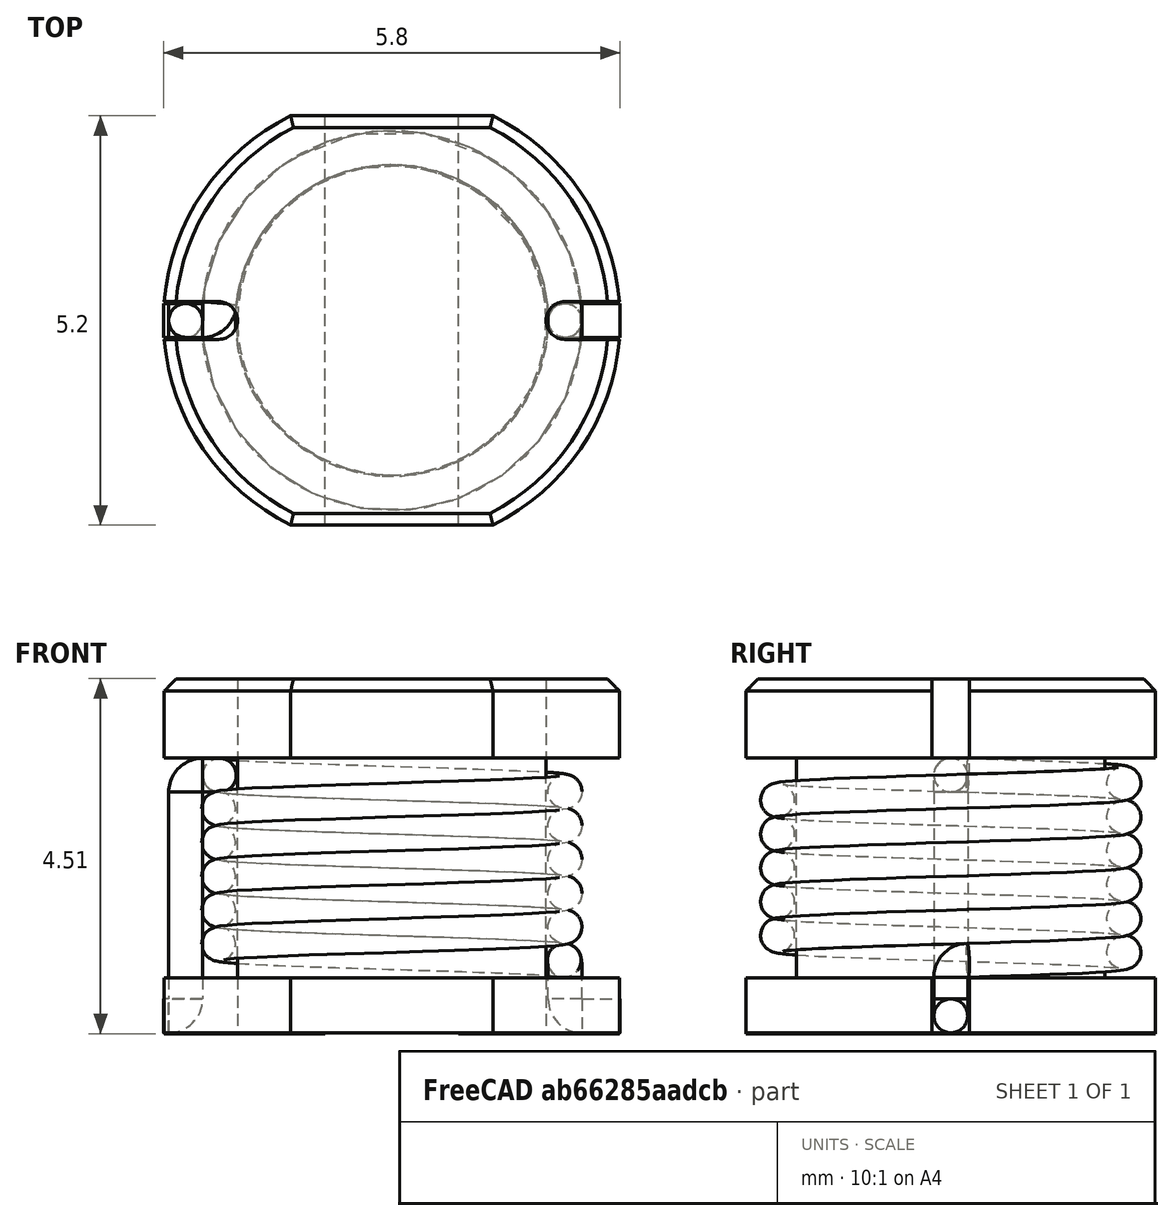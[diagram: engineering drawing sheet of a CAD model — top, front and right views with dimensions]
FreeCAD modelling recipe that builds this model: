
FCSTD DOCUMENT  (FreeCAD 0.17R13528 (Git))
Label: SMD_Inductors_CDxx
License: All rights reserved
LicenseURL: http://en.wikipedia.org/wiki/All_rights_reserved
objects: Part::Part2DObjectPython×19, Part::Sweep×6, Part::Loft×4, Sketcher::SketchObject×3, Part::Extrusion×3, Part::Chamfer×1, Spreadsheet::Sheet×1, Part::Cylinder×1, Part::Helix×1, App::DocumentObjectGroup×1
note: 38 computed .brp shape members not serialized (recipe doc carries the construction recipe); baked Part::Feature solids carry a one-line shape summary decoded from their .brp

FEATURE [Sketcher::SketchObject] Sketch  label="Foundation"
  Placement = pos=(0,0,0) rot=(0,0,1;1.5708rad)
  expr: Constraints.X = Table.X_Foundation
  expr: Constraints.R1 = Table.D_Otv_Vivod / 2
  expr: Constraints.R = Table.D_Foundation / 2
  expr: Constraints.H = Table.D_Coil
  expr: Constraints[27] = Constraints.R
  expr: Constraints[28] = Constraints.R
  sketch-geometry (12):
    g0: LineSegment StartX=-2.6 StartY=1.28452 StartZ=0 EndX=-2.6 EndY=-1.28452 EndZ=0
    g1: LineSegment StartX=2.6 StartY=1.28452 StartZ=0 EndX=2.6 EndY=-1.28452 EndZ=0
    g2: ArcOfCircle CenterX=0 CenterY=0 CenterZ=0 NormalX=0 NormalY=0 NormalZ=1 AngleXU=0 Radius=2.9 StartAngle=1.65365 EndAngle=2.68272
    g3: ArcOfCircle CenterX=0 CenterY=0 CenterZ=0 NormalX=0 NormalY=0 NormalZ=1 AngleXU=0 Radius=2.9 StartAngle=0.458874 EndAngle=1.48794
    g4: ArcOfCircle CenterX=0 CenterY=0 CenterZ=0 NormalX=0 NormalY=0 NormalZ=1 AngleXU=0 Radius=2.9 StartAngle=3.60047 EndAngle=4.62954
    g5: ArcOfCircle CenterX=0 CenterY=0 CenterZ=0 NormalX=0 NormalY=0 NormalZ=1 AngleXU=0 Radius=2.9 StartAngle=4.79524 EndAngle=5.82431
    g6: LineSegment StartX=-0.24 StartY=-2.89005 StartZ=0 EndX=-0.24 EndY=-2.2 EndZ=0
    g7: LineSegment StartX=0.24 StartY=-2.89005 StartZ=0 EndX=0.24 EndY=-2.2 EndZ=0
    g8: LineSegment StartX=-0.24 StartY=2.89005 StartZ=0 EndX=-0.24 EndY=2.2 EndZ=0
    g9: LineSegment StartX=0.24 StartY=2.89005 StartZ=0 EndX=0.24 EndY=2.2 EndZ=0
    g10: ArcOfCircle CenterX=0 CenterY=2.2 CenterZ=0 NormalX=0 NormalY=0 NormalZ=1 AngleXU=0 Radius=0.24 StartAngle=3.14159 EndAngle=6.28319
    g11: ArcOfCircle CenterX=0 CenterY=-2.2 CenterZ=0 NormalX=0 NormalY=0 NormalZ=1 AngleXU=0 Radius=0.24 StartAngle=0 EndAngle=3.14159
  constraints (37):
    c: Vertical(g1)
    c: DistanceX(g0,g1) = 5.2  'X'
    c: Coincident(g2,g-1)
    c: Coincident(g2,g0)
    c: Coincident(g3,g-1)
    c: Coincident(g3,g1)
    c: Coincident(g4,g-1)
    c: Coincident(g4,g0)
    c: Coincident(g5,g-1)
    c: Coincident(g5,g1)
    c: Coincident(g6,g4)
    c: Vertical(g6)
    c: Coincident(g7,g5)
    c: Vertical(g7)
    c: Coincident(g8,g2)
    c: Vertical(g8)
    c: Coincident(g9,g3)
    c: Vertical(g9)
    c: PointOnObject(g10,g-2)
    c: Coincident(g10,g9)
    c: Coincident(g10,g8)
    c: Coincident(g11,g6)
    c: Coincident(g11,g7)
    c: Radius(g10) = 0.24  'R1'
    c: Equal(g10,g11)
    c: Symmetric(g11,g10,g-1)
    c: Radius(g3) = 2.9  'R'
    c: Radius(g2) = 2.9
    c: Radius(g5) = 2.9
    c: Equal(g7,g6)
    c: Equal(g6,g8)
    c: Equal(g8,g9)
    c: Symmetric(g6,g8,g-1)
    c: DistanceY(g11,g10) = 4.4  'H'
    c: DistanceY(g1,g0) = 0
    c: Symmetric(g0,g0,g-1)
    c: DistanceY(g8,g10) = 0
FEATURE [Part::Extrusion] Extrude  label="Foundation_Solid"
  Base = -> Sketch
  Dir = (0,0,1)
  DirMode = 2
  FaceMakerClass = Part::FaceMakerBullseye
  LengthFwd = 0.7
  LengthRev = 0
  Solid = true
  Symmetric = false
  expr: LengthFwd = Table.Th_Foundation
FEATURE [Sketcher::SketchObject] Sketch001  label="Top"
  Placement = pos=(0,0,3.495) rot=(0,0,1;1.5708rad)
  expr: Placement.Base.z = Table.H_Coil - Table.Th_Top
  expr: Constraints[26] = Foundation.Constraints.R
  expr: Constraints[28] = Foundation.Constraints.R
  expr: Constraints[27] = Foundation.Constraints.R
  expr: Constraints[33] = Foundation.Constraints.H
  expr: Constraints[23] = Foundation.Constraints.R1
  expr: Constraints[1] = Foundation.Constraints.X
  sketch-geometry (12):
    g0: LineSegment StartX=-2.6 StartY=1.28452 StartZ=0 EndX=-2.6 EndY=-1.28452 EndZ=0
    g1: LineSegment StartX=2.6 StartY=1.28452 StartZ=0 EndX=2.6 EndY=-1.28452 EndZ=0
    g2: ArcOfCircle CenterX=0 CenterY=0 CenterZ=0 NormalX=0 NormalY=0 NormalZ=1 AngleXU=0 Radius=2.9 StartAngle=1.65365 EndAngle=2.68272
    g3: ArcOfCircle CenterX=0 CenterY=0 CenterZ=0 NormalX=0 NormalY=0 NormalZ=1 AngleXU=0 Radius=2.9 StartAngle=0.458874 EndAngle=1.48794
    g4: ArcOfCircle CenterX=0 CenterY=0 CenterZ=0 NormalX=0 NormalY=0 NormalZ=1 AngleXU=0 Radius=2.9 StartAngle=3.60047 EndAngle=4.62954
    g5: ArcOfCircle CenterX=0 CenterY=0 CenterZ=0 NormalX=0 NormalY=0 NormalZ=1 AngleXU=0 Radius=2.9 StartAngle=4.79524 EndAngle=5.82431
    g6: LineSegment StartX=-0.24 StartY=-2.89005 StartZ=0 EndX=-0.24 EndY=-2.2 EndZ=0
    g7: LineSegment StartX=0.24 StartY=-2.89005 StartZ=0 EndX=0.24 EndY=-2.2 EndZ=0
    g8: LineSegment StartX=-0.24 StartY=2.89005 StartZ=0 EndX=-0.24 EndY=2.2 EndZ=0
    g9: LineSegment StartX=0.24 StartY=2.89005 StartZ=0 EndX=0.24 EndY=2.2 EndZ=0
    g10: ArcOfCircle CenterX=0 CenterY=2.2 CenterZ=0 NormalX=0 NormalY=0 NormalZ=1 AngleXU=0 Radius=0.24 StartAngle=3.14159 EndAngle=6.28319
    g11: ArcOfCircle CenterX=0 CenterY=-2.2 CenterZ=0 NormalX=0 NormalY=0 NormalZ=1 AngleXU=0 Radius=0.24 StartAngle=0 EndAngle=3.14159
  constraints (37):
    c: Vertical(g1)
    c: DistanceX(g0,g1) = 5.2
    c: Coincident(g2,g-1)
    c: Coincident(g2,g0)
    c: Coincident(g3,g-1)
    c: Coincident(g3,g1)
    c: Coincident(g4,g-1)
    c: Coincident(g4,g0)
    c: Coincident(g5,g-1)
    c: Coincident(g5,g1)
    c: Coincident(g6,g4)
    c: Vertical(g6)
    c: Coincident(g7,g5)
    c: Vertical(g7)
    c: Coincident(g8,g2)
    c: Vertical(g8)
    c: Coincident(g9,g3)
    c: Vertical(g9)
    c: PointOnObject(g10,g-2)
    c: Coincident(g10,g9)
    c: Coincident(g10,g8)
    c: Coincident(g11,g6)
    c: Coincident(g11,g7)
    c: Radius(g10) = 0.24
    c: Equal(g10,g11)
    c: Symmetric(g11,g10,g-1)
    c: Radius(g3) = 2.9
    c: Radius(g2) = 2.9
    c: Radius(g5) = 2.9
    c: Equal(g7,g6)
    c: Equal(g6,g8)
    c: Equal(g8,g9)
    c: Symmetric(g6,g8,g-1)
    c: DistanceY(g11,g10) = 4.4
    c: DistanceY(g1,g0) = 0
    c: Symmetric(g0,g0,g-1)
    c: DistanceY(g8,g10) = 0
FEATURE [Part::Extrusion] Extrude001  label="Top_Solid"
  Base = -> Sketch001
  Dir = (0,0,1)
  DirMode = 2
  FaceMakerClass = Part::FaceMakerBullseye
  LengthFwd = 1
  LengthRev = 0
  Solid = true
  Symmetric = false
  expr: LengthFwd = Table.Th_Top
FEATURE [Part::Chamfer] Chamfer  label="Top_Chamfer_Solid"
  Base = -> Extrude001
  Edges = 6 edges r=0.15: [Edge4,Edge7,Edge10,Edge22,Edge25,Edge28]
FEATURE [Spreadsheet::Sheet] Spreadsheet  label="Table"
  cells = A1=Диаметр катушки по центу провода; B1(D_Coil)==Table.X_Foundation - 0.80000000000000004mm; C1="D_Coil"; D1=Diameter of coil in the center of the wire; A2=Толщина провода; B2(Th_Wire)==0.42999999999999999mm; C2="Th_Wire"; D2=Thickness of wire; A3=Основание; A4=Толщина основания; B4(Th_Foundation)==0.69999999999999996mm; C4="Th_Foundation"; D4=Foundation height; A5=Диаметр основания; B5(D_Foundation)==5.7999999999999998mm; C5="D_Foundation"; D5=Foundation diameter; A6=Растояние между фасками; B6(X_Foundation)==5.2000000000000002mm; C6="X_Foundation"; D6=Foundation "A" dimension; A7=Диаметр отверстий для выводов (расчитываеться, можно ввести); B7(D_Otv_Vivod)==Th_Wire + 0.050000000000000003mm; C7="D_Otv_Vivod"; D7=Diameter of holes for pinouts (calculated, can be setted); A8=Крышка; A9=Толщина крышки; B9(Th_Top)==1mm; C9="Th_Top"; D9=Top height; A10=Высота катушки (расчитывается); B10(H_Coil)==Table.Th_Foundation + (Table.KolvoVitkov + 1.5) * Table.Th_Wire + Table.Th_Top; C10="H_Coil"; D10=Inductor height (calculated); A12=Количество витков; B12(KolvoVitkov)=5; C12="KolvoVitkov"; D12=Number of turns; A13=Ширина площадок; B13(E_dimension)==Table.X_Foundation; C13="E_dimension"; D13=Pinouts "E" dimension; A14=Отступ площадок от центра; B14(F_dimension)==1.7mm; C14="F_dimension"; D14=Pinouts "E" dimension; A15=Длина окружности в плоскости (от диметра катушки); B15(L_Okr)==pi * Table.D_Coil; C15="L_Okr"; D15=Circumference; A16=Длина провода на один виток; B16(L_1Wire)==sqrt(Table.L_Okr * Table.L_Okr + Table.Th_Wire * Table.Th_Wire); C16="L_1Wire"; A17=На сколько повернуть круг; B17(Ugol1)==90deg - asin(Table.Th_Wire / Table.L_1Wire); C17="Ugol1"; A18=Узнаем на сколько повернуть спираль против час стрелки вокруг оси Z; A19=Повернуть спираль вокруг OZ на; B19(Ugol2)==180deg - 2 * acos(Table.Th_Wire / 2 / Table.D_Coil); C19="Ugol2"; A20=Спираль надо приподнять вот на эту величину; B20(DeltaH)==Table.Th_Wire * Table.Ugol2 / 360deg; C20="DeltaH"; D20=Спираль станет короче на величину в 2 раза большую; A22=Расчеты координат и поворота круга для постройки спирали провода; A23=Поворот на угол фи вокруг оси OZ; B23(fi)==Table.Ugol2; C23="fi"; A24=Поворот на угол тета вокруг повернутой оси OU; B24(teta)==90deg + asin(Table.Th_Wire / Table.L_1Wire); C24="teta"; A25=Поворот на угол пси вокруг повернутой оси OW; B25(psii)==0deg; C25="psii" Если сделаем провод прям. сечения; A26=Результирующая матрица поворота; A27(M_11)==cos(Table.fi) * cos(Table.psii) - sin(Table.fi) * cos(Table.teta) * sin(Table.psii); B27(M_21)==-cos(Table.fi) * sin(Table.psii) - sin(Table.fi) * cos(Table.teta) * cos(Table.psii); C27(M_31)==sin(Table.fi) * sin(Table.teta); A28(M_12)==sin(Table.fi) * cos(Table.psii) + cos(Table.fi) * cos(Table.teta) * sin(Table.psii); B28(M_22)==-sin(Table.fi) * sin(Table.psii) + cos(Table.fi) * cos(Table.teta) * cos(Table.psii); C28(M_32)==-cos(Table.fi) * sin(Table.teta); A29(M_13)==sin(Table.teta) * sin(Table.psii); B29(M_23)==sin(Table.teta) * cos(Table.psii); C29(M_33)==cos(Table.teta); A30=Угол на который надо поворачивать; B30(Ugol3)==acos((Table.M_11 + Table.M_22 + Table.M_33 - 1) * 0.5); C30="Ugol3"; A31=Вектор вокруг которого надо поворачивать, X; B31(V_X)==-1 / (2 * sin(Table.Ugol3)) * (Table.M_32 - Table.M_23); C31="V_X"; A32=Вектор вокруг которого надо поворачивать, Y; B32(V_Y)==-1 / (2 * sin(Table.Ugol3)) * (Table.M_13 - Table.M_31); C32="V_Y"; A33=Вектор вокруг которого надо поворачивать, Z; B33(V_Z)==-1 / (2 * sin(Table.Ugol3)) * (Table.M_21 - Table.M_12); C33="V_Z"; A34=Кординаты вектора до центра круга до/после пов., X; B34==Table.D_Coil / 2; C34(Center1_X)==Table.D_Coil / 2 * cos(Table.fi); A35=Кординаты вектора до центра круга до/после пов., Y; B35==0mm; C35(Center1_Y)==Table.D_Coil / 2 * sin(Table.fi); A36=Кординаты вектора до центра круга до/после пов., Z; B36==Table.Th_Foundation + Table.Th_Wire / 2; C36(Center1_Z)==Table.Th_Foundation + Th_Wire / 2 + Table.DeltaH; A37=Расчет координат поворота дуги; A38=Поворот на угол фи вокруг оси OZ; B38(fi2)==-Table.Ugol2; C38="fi2"; A39=Поворот на угол тета вокруг повернутой оси OU; B39(teta2)==90deg - asin(Table.Th_Wire / Table.L_1Wire); C39="teta2"; A40=Поворот на угол пси вокруг повернутой оси OW; B40(psi2)==0deg; C40="psi2"; A41=Результирующая матрица поворота Дуга в начале; A42==cos(fi2) * cos(psi2) - sin(fi2) * cos(teta2) * sin(psi2); B42==-cos(fi2) * sin(psi2) - sin(fi2) * cos(teta2) * cos(psi2); C42==sin(fi2) * sin(teta2); A43==sin(fi2) * cos(psi2) + cos(fi2) * cos(teta2) * sin(psi2); B43==-sin(fi2) * sin(psi2) + cos(fi2) * cos(teta2) * cos(psi2); C43==-cos(fi2) * sin(teta2); A44==sin(teta2) * sin(psi2); B44==sin(teta2) * cos(psi2); C44==cos(teta2); A45=Угол на который надо поворачивать; B45(Ugol4)==acos((A42 + B43 + C44 - 1) * 0.5); C45="Ugol4"; A46=Вектор вокруг которого надо поворачивать, X; B46(V2_X)==-1 / (2 * sin(Table.Ugol4)) * (C43 - B44); C46="V2_X"; A47=Вектор вокруг которого надо поворачивать, Y; B47(V2_Y)==-1 / (2 * sin(Ugol4)) * (A44 - C42); C47="V2_Y"; A48=Вектор вокруг которого надо поворачивать, Z; B48(V2_Z)==-1 / (2 * sin(Ugol4)) * (B42 - A43); C48="V2_Z"; A49=Результирующая матрица поворота Дуга в конце; B49(teta3)==asin(Th_Wire / sqrt(L_Okr * L_Okr + Th_Wire * Th_Wire)); C49="teta3"; A50==cos(90deg + fi) * cos(psi2) - sin(90deg + fi) * cos(90deg) * sin(psi2); B50==-cos(90deg + fi) * sin(psi2) - sin(90deg + fi) * cos(90deg) * cos(psi2); C50==sin(90deg + fi) * sin(90deg); A51==sin(90deg + fi) * cos(psi2) + cos(90deg + fi) * cos(90deg) * sin(psi2); B51==-sin(90deg + fi) * sin(psi2) + cos(90deg + fi) * cos(90deg) * cos(psi2); C51==-cos(90deg + fi) * sin(90deg); A52==sin(90deg) * sin(psi2); B52==sin(90deg) * cos(psi2); C52==cos(90deg); A53=Угол на который надо поворачивать; B53(Ugol5)==acos((A50 + B51 + C52 - 1) * 0.5); C53="Ugol5"; A54=Вектор вокруг которого надо поворачивать, X; B54(V3_X)==-1 / (2 * sin(Ugol5)) * (C51 - B52); C54="V3_X"; A55=Вектор вокруг которого надо поворачивать, Y; B55(V3_Y)==-1 / (2 * sin(Ugol5)) * (A52 - C50); C55="V3_Y"; A56=Вектор вокруг которого надо поворачивать, Z; B56(V3_Z)==-1 / (2 * sin(Ugol5)) * (B50 - A51); C56="V3_Z"
FEATURE [Part::Cylinder] Cylinder
  Angle = 360
  AttacherType = Attacher::AttachEngine3D
  Height = 2.795
  Placement = pos=(0,0,0.7) rot=(0,0,1;0rad)
  Radius = 1.96
  expr: Height = Table.H_Coil - Table.Th_Foundation - Table.Th_Top
  expr: Radius = (Table.D_Coil - Table.D_Otv_Vivod) / 2
  expr: Placement.Base.z = Table.Th_Foundation
FEATURE [Part::Helix] Helix
  Angle = 0
  AttacherType = Attacher::AttachEngine3D
  Height = 2.35162
  LocalCoord = 0
  Pitch = 0.43
  Placement = pos=(0,0,0.921691) rot=(0,0,1;0.097766rad)
  Radius = 2.2
  Style = 1
  expr: Placement.Rotation.Angle = Table.Ugol2
  expr: Pitch = Table.Th_Wire
  expr: Height = Table.H_Coil - Table.Th_Foundation - Table.Th_Top - Table.Th_Wire - Table.DeltaH * 2
  expr: Placement.Base.z = Table.Th_Foundation + Table.Th_Wire / 2 + Table.DeltaH
  expr: Radius = Table.D_Coil / 2
FEATURE [Part::Part2DObjectPython] Circle001  label="Circle2"  # Draft 2D object (typed FeaturePython)
  FirstAngle = 0
  LastAngle = 0
  MakeFace = true
  Placement = pos=(2.2,0,0.706691) rot=(0,0,1;0rad)
  Radius = 0.215
  expr: Radius = Table.Th_Wire / 2
  expr: Placement.Base.z = Table.Th_Foundation + Table.DeltaH
  expr: Placement.Base.x = Table.D_Coil / 2
FEATURE [Part::Part2DObjectPython] Circle002  label="Circle3"  # Draft 2D object (typed FeaturePython)
  FirstAngle = 0
  LastAngle = 0
  MakeFace = true
  Placement = pos=(2.2,0,0.43) rot=(0,0,1;0rad)
  Radius = 0.215
  expr: Radius = Table.Th_Wire / 2
  expr: Placement.Base.z = Table.Th_Wire
  expr: Placement.Base.x = Table.D_Coil / 2
FEATURE [Part::Part2DObjectPython] Circle003  label="Circle4"  # Draft 2D object (typed FeaturePython)
  FirstAngle = 0
  LastAngle = 0
  MakeFace = true
  Placement = pos=(2.415,0,0.215) rot=(0,1,0;1.5708rad)
  Radius = 0.215
  expr: Placement.Base.x = (Table.D_Coil + Table.Th_Wire) / 2
  expr: Radius = Table.Th_Wire / 2
  expr: Placement.Base.z = Table.Th_Wire / 2
FEATURE [Part::Part2DObjectPython] Circle004  label="RotateCircle"  # Draft 2D object (typed FeaturePython)
  FirstAngle = 0
  LastAngle = 0
  MakeFace = true
  Placement = pos=(2.18949,0.214743,0.921691) rot=(0.997687,0.048806,0.047309;1.60421rad)
  Radius = 0.215
  expr: Placement.Base.x = Table.Center1_X
  expr: Placement.Base.y = Table.Center1_Y
  expr: Placement.Rotation.Axis.z = Table.V_Z
  expr: Placement.Rotation.Axis.y = Table.V_Y
  expr: Placement.Base.z = Table.Center1_Z
  expr: Placement.Rotation.Angle = Table.Ugol3
  expr: Placement.Rotation.Axis.x = Table.V_X
  expr: Radius = Table.Th_Wire / 2
FEATURE [Part::Part2DObjectPython] Arc  label="Arc2"  # Draft 2D object (typed FeaturePython)
  FirstAngle = 90
  LastAngle = 180
  MakeFace = true
  Placement = pos=(2.18949,0.214743,0.706691) rot=(0.539926,0.595289,0.595072;2.15173rad)
  Radius = 0.215
  expr: Placement.Base.y = Table.Center1_Y
  expr: Radius = Table.Th_Wire / 2
  expr: Placement.Rotation.Axis.z = Table.V3_Z
  expr: Placement.Rotation.Axis.y = Table.V3_Y
  expr: Placement.Rotation.Angle = Table.Ugol5
  expr: Placement.Rotation.Axis.x = Table.V3_X
  expr: Placement.Base.z = Table.Th_Foundation + Table.DeltaH
  expr: Placement.Base.x = Table.Center1_X
FEATURE [Part::Part2DObjectPython] Circle005  label="RotateCircle2"  # Draft 2D object (typed FeaturePython)
  FirstAngle = 0
  LastAngle = 0
  MakeFace = true
  Placement = pos=(2.18949,0.214743,0.921691) rot=(0.997687,0.048806,0.047309;1.60421rad)
  Radius = 0.215
  expr: Placement.Base.y = Table.Center1_Y
  expr: Placement.Rotation.Axis.z = Table.V_Z
  expr: Placement.Rotation.Axis.y = Table.V_Y
  expr: Placement.Base.z = Table.Center1_Z
  expr: Placement.Base.x = Table.Center1_X
  expr: Placement.Rotation.Angle = Table.Ugol3
  expr: Placement.Rotation.Axis.x = Table.V_X
  expr: Radius = Table.Th_Wire / 2
FEATURE [Part::Sweep] Sweep001  label="Wire4"
  Frenet = true
  Sections = -> [Circle005,Circle001]
  Solid = true
  Spine = -> Arc [Edge1]
  Transition = 1
FEATURE [Part::Part2DObjectPython] Circle006  label="Circle5"  # Draft 2D object (typed FeaturePython)
  FirstAngle = 0
  LastAngle = 0
  MakeFace = true
  Placement = pos=(2.2,0,0.706691) rot=(0,0,1;0rad)
  Radius = 0.215
  expr: Radius = Table.Th_Wire / 2
  expr: Placement.Base.z = Table.Th_Foundation + Table.DeltaH
  expr: Placement.Base.x = Table.D_Coil / 2
FEATURE [Part::Loft] Loft  label="Wire3"
  Closed = false
  MaxDegree = 5
  Ruled = false
  Sections = -> [Circle002,Circle006]
  Solid = true
FEATURE [Part::Part2DObjectPython] Circle007  label="Circle6"  # Draft 2D object (typed FeaturePython)
  FirstAngle = 0
  LastAngle = 0
  MakeFace = true
  Placement = pos=(2.2,0,0.43) rot=(0,0,1;0rad)
  Radius = 0.215
  expr: Radius = Table.Th_Wire / 2
  expr: Placement.Base.z = Table.Th_Wire
  expr: Placement.Base.x = Table.D_Coil / 2
FEATURE [Part::Part2DObjectPython] Arc001  label="Arc1"  # Draft 2D object (typed FeaturePython)
  FirstAngle = 180
  LastAngle = 270
  MakeFace = true
  Placement = pos=(2.415,0,0.43) rot=(1,0,0;1.5708rad)
  Radius = 0.215
  expr: Placement.Base.z = Table.Th_Wire
  expr: Placement.Base.x = Table.D_Coil / 2 + Table.Th_Wire / 2
  expr: Radius = Table.Th_Wire / 2
FEATURE [Part::Sweep] Sweep002  label="Wire2"
  Frenet = true
  Sections = -> [Circle007,Circle003]
  Solid = true
  Spine = -> Arc001 [Edge1]
  Transition = 1
FEATURE [Part::Sweep] Sweep  label="Wire5"
  Frenet = true
  Sections = -> [Circle004]
  Solid = true
  Spine = -> Helix [Edge1,Edge2,Edge3,Edge4,Edge5,Edge6]
  Transition = 1
FEATURE [Part::Part2DObjectPython] Arc002  label="Arc3"  # Draft 2D object (typed FeaturePython)
  FirstAngle = 270
  LastAngle = 360
  MakeFace = true
  Placement = pos=(-2.40449,0.214743,3.27331) rot=(0,0,1;0rad)
  Radius = 0.215
  expr: Radius = Table.Th_Wire / 2
  expr: Placement.Base.y = Table.Center1_Y
  expr: Placement.Base.z = Table.H_Coil - Table.Th_Top - Table.Th_Wire / 2 - Table.DeltaH
  expr: Placement.Base.x = -Table.Center1_X - Table.Th_Wire / 2
FEATURE [Part::Part2DObjectPython] Circle  # Draft 2D object (typed FeaturePython)
  FirstAngle = 0
  LastAngle = 0
  MakeFace = true
  Placement = pos=(-2.40449,0,3.27331) rot=(0.57735,0.57735,0.57735;2.0944rad)
  Radius = 0.215
  expr: Radius = Table.Th_Wire / 2
  expr: Placement.Base.z = Table.H_Coil - Table.Th_Top - Table.Th_Wire / 2 - Table.DeltaH
  expr: Placement.Base.x = -Table.Center1_X - Table.Th_Wire / 2
FEATURE [Part::Part2DObjectPython] Circle008  label="RotateCircle3"  # Draft 2D object (typed FeaturePython)
  FirstAngle = 0
  LastAngle = 0
  MakeFace = true
  Placement = pos=(-2.18949,0.214743,3.27331) rot=(0.997539,-0.048799,-0.050338;1.54216rad)
  Radius = 0.215
  expr: Placement.Rotation.Axis.z = Table.V2_Z
  expr: Placement.Rotation.Axis.y = Table.V2_Y
  expr: Placement.Rotation.Angle = Table.Ugol4
  expr: Placement.Rotation.Axis.x = Table.V2_X
  expr: Placement.Base.y = Table.Center1_Y
  expr: Radius = Table.Th_Wire / 2
  expr: Placement.Base.z = Table.H_Coil - Table.Th_Top - Table.Th_Wire / 2 - Table.DeltaH
  expr: Placement.Base.x = -Table.Center1_X
FEATURE [Part::Sweep] Sweep003  label="Wire6"
  Frenet = true
  Sections = -> [Circle008,Circle]
  Solid = true
  Spine = -> Arc002 [Edge1]
  Transition = 1
FEATURE [Part::Part2DObjectPython] Arc003  label="Arc4"  # Draft 2D object (typed FeaturePython)
  FirstAngle = 90
  LastAngle = 180
  MakeFace = true
  Placement = pos=(-2.40449,0,3.05831) rot=(1,0,0;1.5708rad)
  Radius = 0.215
  expr: Placement.Base.z = Table.H_Coil - Table.Th_Top - Table.Th_Wire - Table.DeltaH
  expr: Radius = Table.Th_Wire / 2
  expr: Placement.Base.x = -Table.Center1_X - Table.Th_Wire / 2
FEATURE [Part::Part2DObjectPython] Circle009  # Draft 2D object (typed FeaturePython)
  FirstAngle = 0
  LastAngle = 0
  MakeFace = true
  Placement = pos=(-2.61949,0,3.05831) rot=(0,0,1;0rad)
  Radius = 0.215
  expr: Radius = Table.Th_Wire / 2
  expr: Placement.Base.z = Table.H_Coil - Table.Th_Top - Table.Th_Wire - Table.DeltaH
  expr: Placement.Base.x = -Table.Center1_X - Table.Th_Wire
FEATURE [Part::Part2DObjectPython] Circle010  # Draft 2D object (typed FeaturePython)
  FirstAngle = 0
  LastAngle = 0
  MakeFace = true
  Placement = pos=(-2.61949,0,0.43) rot=(0,0,1;0rad)
  Radius = 0.215
  expr: Radius = Table.Th_Wire / 2
  expr: Placement.Base.z = Table.Th_Wire
  expr: Placement.Base.x = -Table.Center1_X - Table.Th_Wire
FEATURE [Part::Sweep] Sweep004  label="Wire7"
  Frenet = true
  Sections = -> [Circle,Circle009]
  Solid = true
  Spine = -> Arc003 [Edge1]
  Transition = 1
FEATURE [Part::Part2DObjectPython] Circle011  # Draft 2D object (typed FeaturePython)
  FirstAngle = 0
  LastAngle = 0
  MakeFace = true
  Placement = pos=(-2.83449,0,0.215) rot=(0,1,0;1.5708rad)
  Radius = 0.215
  expr: Radius = Table.Th_Wire / 2
  expr: Placement.Base.z = Table.Th_Wire / 2
  expr: Placement.Base.x = -Table.Center1_X - Table.Th_Wire * 3 / 2
FEATURE [Part::Loft] Loft001  label="Wire8"
  Closed = false
  MaxDegree = 5
  Ruled = false
  Sections = -> [Circle009,Circle010]
  Solid = true
FEATURE [Part::Part2DObjectPython] Arc004  label="Arc5"  # Draft 2D object (typed FeaturePython)
  FirstAngle = 270
  LastAngle = 360
  MakeFace = true
  Placement = pos=(-2.83449,0,0.43) rot=(1,0,0;1.5708rad)
  Radius = 0.215
  expr: Placement.Base.z = Table.Th_Wire
  expr: Radius = Table.Th_Wire / 2
  expr: Placement.Base.x = -Table.Center1_X - Table.Th_Wire * 3 / 2
FEATURE [Part::Sweep] Sweep005  label="Wire9"
  Frenet = true
  Sections = -> [Circle010,Circle011]
  Solid = true
  Spine = -> Arc004 [Edge1]
  Transition = 1
FEATURE [Part::Part2DObjectPython] Circle012  # Draft 2D object (typed FeaturePython)
  FirstAngle = 0
  LastAngle = 0
  MakeFace = true
  Placement = pos=(2.9,0,0.215) rot=(0,1,0;1.5708rad)
  Radius = 0.215
  expr: Placement.Base.x = Table.D_Foundation / 2
  expr: Radius = Table.Th_Wire / 2
  expr: Placement.Base.z = Table.Th_Wire / 2
FEATURE [Part::Loft] Loft002  label="Wire1"
  Closed = false
  MaxDegree = 5
  Ruled = false
  Sections = -> [Circle003,Circle012]
  Solid = true
FEATURE [Part::Part2DObjectPython] Circle013  # Draft 2D object (typed FeaturePython)
  FirstAngle = 0
  LastAngle = 0
  MakeFace = true
  Placement = pos=(-2.9,0,0.215) rot=(0,1,0;1.5708rad)
  Radius = 0.215
  expr: Radius = Table.Th_Wire / 2
  expr: Placement.Base.z = Table.Th_Wire / 2
  expr: Placement.Base.x = -Table.D_Foundation / 2
FEATURE [Part::Loft] Loft003  label="Wire10"
  Closed = false
  MaxDegree = 5
  Ruled = false
  Sections = -> [Circle011,Circle013]
  Solid = true
FEATURE [App::DocumentObjectGroup] ____________  label="Wire"
  Group = -> [Loft002,Sweep002,Loft,Sweep001,Sweep,Sweep003,Sweep004,Loft001,Sweep005,Loft003,Arc001,Arc,Arc002,Arc003,Arc004,Helix]
FEATURE [Sketcher::SketchObject] Sketch002  label="Pinouts"
  Placement = pos=(0,0,0) rot=(0,0,1;1.5708rad)
  expr: Constraints[47] = Table.F_dimension
  expr: Constraints[32] = Table.D_Foundation / 2
  expr: Constraints[0] = Table.E_dimension
  expr: Constraints[18] = Table.D_Otv_Vivod / 2
  expr: Constraints[25] = Table.D_Coil
  sketch-geometry (16):
    g0: ArcOfCircle CenterX=0 CenterY=0 CenterZ=0 NormalX=0 NormalY=0 NormalZ=1 AngleXU=0 Radius=2.9 StartAngle=1.65365 EndAngle=2.68272
    g1: ArcOfCircle CenterX=0 CenterY=0 CenterZ=0 NormalX=0 NormalY=0 NormalZ=1 AngleXU=0 Radius=2.9 StartAngle=0.458874 EndAngle=1.48794
    g2: ArcOfCircle CenterX=0 CenterY=0 CenterZ=0 NormalX=0 NormalY=0 NormalZ=1 AngleXU=0 Radius=2.9 StartAngle=3.60047 EndAngle=4.62954
    g3: ArcOfCircle CenterX=0 CenterY=0 CenterZ=0 NormalX=0 NormalY=0 NormalZ=1 AngleXU=0 Radius=2.9 StartAngle=4.79524 EndAngle=5.82431
    g4: LineSegment StartX=-0.24 StartY=-2.89005 StartZ=0 EndX=-0.24 EndY=-2.2 EndZ=0
    g5: LineSegment StartX=0.24 StartY=-2.89005 StartZ=0 EndX=0.24 EndY=-2.2 EndZ=0
    g6: LineSegment StartX=-0.24 StartY=2.89005 StartZ=0 EndX=-0.24 EndY=2.2 EndZ=0
    g7: LineSegment StartX=0.24 StartY=2.89005 StartZ=0 EndX=0.24 EndY=2.2 EndZ=0
    g8: ArcOfCircle CenterX=0 CenterY=2.2 CenterZ=0 NormalX=0 NormalY=0 NormalZ=1 AngleXU=0 Radius=0.24 StartAngle=3.14159 EndAngle=6.28319
    g9: ArcOfCircle CenterX=0 CenterY=-2.2 CenterZ=0 NormalX=0 NormalY=0 NormalZ=1 AngleXU=0 Radius=0.24 StartAngle=0 EndAngle=3.14159
    g10: LineSegment StartX=2.6 StartY=1.28452 StartZ=0 EndX=2.6 EndY=0.85 EndZ=0
    g11: LineSegment StartX=-2.6 StartY=0.85 StartZ=0 EndX=-2.6 EndY=1.28452 EndZ=0
    g12: LineSegment StartX=-2.6 StartY=-1.28452 StartZ=0 EndX=-2.6 EndY=-0.85 EndZ=0
    g13: LineSegment StartX=2.6 StartY=-1.28452 StartZ=0 EndX=2.6 EndY=-0.85 EndZ=0
    g14: LineSegment StartX=-2.6 StartY=-0.85 StartZ=0 EndX=2.6 EndY=-0.85 EndZ=0
    g15: LineSegment StartX=-2.6 StartY=0.85 StartZ=0 EndX=2.6 EndY=0.85 EndZ=0
  constraints (49):
    c: DistanceX(g2,g3) = 5.2
    c: Coincident(g0,g-1)
    c: Coincident(g1,g-1)
    c: Coincident(g2,g-1)
    c: Coincident(g3,g-1)
    c: Coincident(g4,g2)
    c: Vertical(g4)
    c: Coincident(g5,g3)
    c: Vertical(g5)
    c: Coincident(g6,g0)
    c: Vertical(g6)
    c: Coincident(g7,g1)
    c: Vertical(g7)
    c: PointOnObject(g8,g-2)
    c: Coincident(g8,g7)
    c: Coincident(g8,g6)
    c: Coincident(g9,g4)
    c: Coincident(g9,g5)
    c: Radius(g8) = 0.24
    c: Equal(g8,g9)
    c: Symmetric(g9,g8,g-1)
    c: Equal(g5,g4)
    c: Equal(g4,g6)
    c: Equal(g6,g7)
    c: Symmetric(g4,g6,g-1)
    c: DistanceY(g9,g8) = 4.4
    c: DistanceY(g3,g2) = 0
    c: DistanceY(g6,g8) = 0
    c: Coincident(g10,g1)
    c: Vertical(g10)
    c: Coincident(g11,g0)
    c: Vertical(g11)
    c: Radius(g1) = 2.9
    c: Equal(g1,g0)
    c: Equal(g1,g2)
    c: Equal(g1,g3)
    c: Coincident(g12,g2)
    c: Vertical(g12)
    c: Coincident(g13,g3)
    c: Vertical(g13)
    c: Symmetric(g2,g0,g-1)
    c: Horizontal(g14)
    c: Coincident(g13,g14)
    c: Coincident(g12,g14)
    c: Horizontal(g15)
    c: Coincident(g10,g15)
    c: Coincident(g11,g15)
    c: DistanceY(g13,g10) = 1.7
    c: Symmetric(g10,g13,g-1)
FEATURE [Part::Extrusion] Extrude002  label="Pinouts_Solid"
  Base = -> Sketch002
  Dir = (0,0,1)
  DirMode = 2
  FaceMakerClass = Part::FaceMakerBullseye
  LengthFwd = 0.01
  LengthRev = 0
  Reversed = true
  Solid = true
  Symmetric = false
